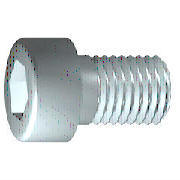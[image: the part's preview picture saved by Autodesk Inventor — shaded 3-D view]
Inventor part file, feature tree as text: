
AUTODESK INVENTOR PART (.ipt)
format: ipt  version: 2015 SP1 (Build 190203100, 203)  size: 187,904 bytes
history: native  units: mm (DEFAULTED — no unit token found)
features: sketch x2, extrude x1, plane x1, fillet x1
ambient origin geometry x7: Origin, YZ Plane, XY Plane, X Axis, Y Axis, Z Axis, Center Point
bodies: Solid1 (feature_tree), Body (feature_tree)
feature tree (5):
  extrude  "Slot"  Depth=6.0mm
  plane  "Work Plane1"
  fillet  "Fillet2"  Radius=6.0mm
  sketch  "Sketch1"  dims[d1=18.0mm d2=0.61355mm d3=6.0mm]
  sketch  "Sketch2"  dims[d4=3.0mm d5=60.0deg d6=6.0mm d7=6.0mm d8=5.773503mm d9=10.0mm d10=90.0deg d11=10.0mm d12=0.0mm d13=18.0mm d14=0.0mm d15=0.61345mm d16=0.61345mm d17=0.6mm d19=0.0mm d26=30.0mm d27=45.0deg d28=0.0mm d29=0.0mm d30=0.1mm]
